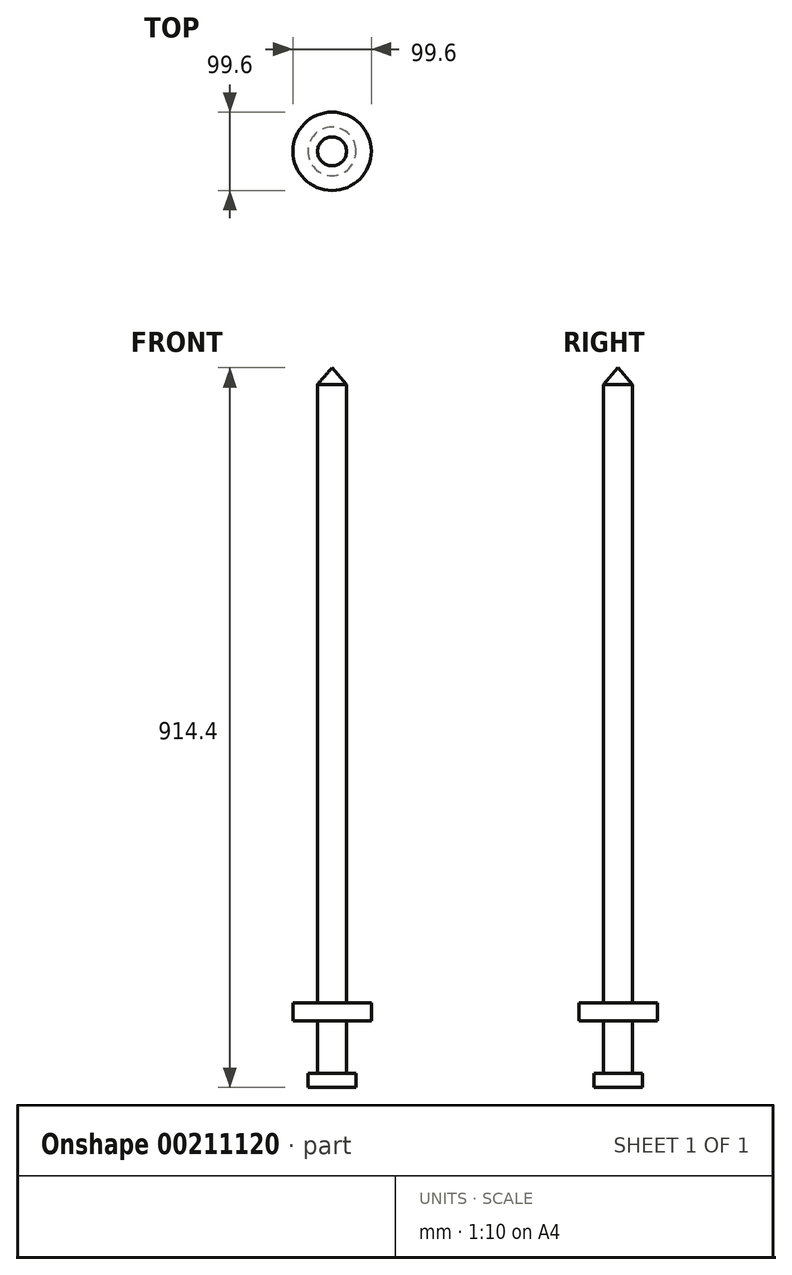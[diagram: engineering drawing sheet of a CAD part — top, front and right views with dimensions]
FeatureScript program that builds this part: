
annotation { "Feature Type Name" : "Feature", "Feature Type Description" : "" }
export const myFeature = defineFeature(function(context is Context, id is Id, definition is map)
    precondition{}
    {
        {
            var Q0;
            Q0=qCreatedBy(makeId("Right.planeOp"),FACE);
            var sketch = newSketch(context, id + "F0", { "sketchPlane" : qUnion([Q0])});
            skLineSegment(sketch, "E0", {"start": v(0, 0) * mm, "end": v(0, 914.4) * mm, "construction": true});
            skLineSegment(sketch, "E1", {"start": v(0, 0) * mm, "end": v(30.7, 0) * mm});
            skLineSegment(sketch, "E2", {"start": v(30.7, 0) * mm, "end": v(30.7, 17.71) * mm});
            skLineSegment(sketch, "E3", {"start": v(30.7, 17.71) * mm, "end": v(18.37, 17.71) * mm});
            skLineSegment(sketch, "E4", {"start": v(18.37, 17.71) * mm, "end": v(18.37, 84.8) * mm});
            skLineSegment(sketch, "E5", {"start": v(18.37, 84.8) * mm, "end": v(49.8, 84.8) * mm});
            skLineSegment(sketch, "E6", {"start": v(49.8, 84.8) * mm, "end": v(49.8, 107.51) * mm});
            skLineSegment(sketch, "E7", {"start": v(49.8, 107.51) * mm, "end": v(18.37, 107.51) * mm});
            skLineSegment(sketch, "E8", {"start": v(18.37, 107.51) * mm, "end": v(18.37, 893.16) * mm});
            skLineSegment(sketch, "E9", {"start": v(18.37, 893.16) * mm, "end": v(0, 914.4) * mm});
            skLineSegment(sketch, "E10", {"start": v(0, 0) * mm, "end": v(0, 914.4) * mm});
            skSolve(sketch);
        }
        {
            var Q0;
            Q0=qCreatedBy(makeId("Right.planeOp"),FACE);
            var sketch = newSketch(context, id + "F1", { "sketchPlane" : qUnion([Q0])});
            skLineSegment(sketch, "E11", {"start": v(0, -8.3) * mm, "end": v(0, 938.33) * mm});
            skSolve(sketch);
        }
        {
            var Q0;
            Q0=makeQuery(id+"F0.imprint","IMPRINT",FACE,{"disambiguationData":[TD([[makeQuery(id+"F0.imprint","IMPRINT",EDGE,{"derivedFrom":sQuery(id+"F0.wireOp",EDGE,"E1")}),1.0]])]});
            var Q1;
            Q1=sQuery(id+"F1.wireOp",EDGE,"E11");
            revolve(context, id + "F2", {"entities" : qUnion([Q0]), "axis" : qUnion([Q1]), "revolveType" : RevolveType.FULL});
        }
    });
